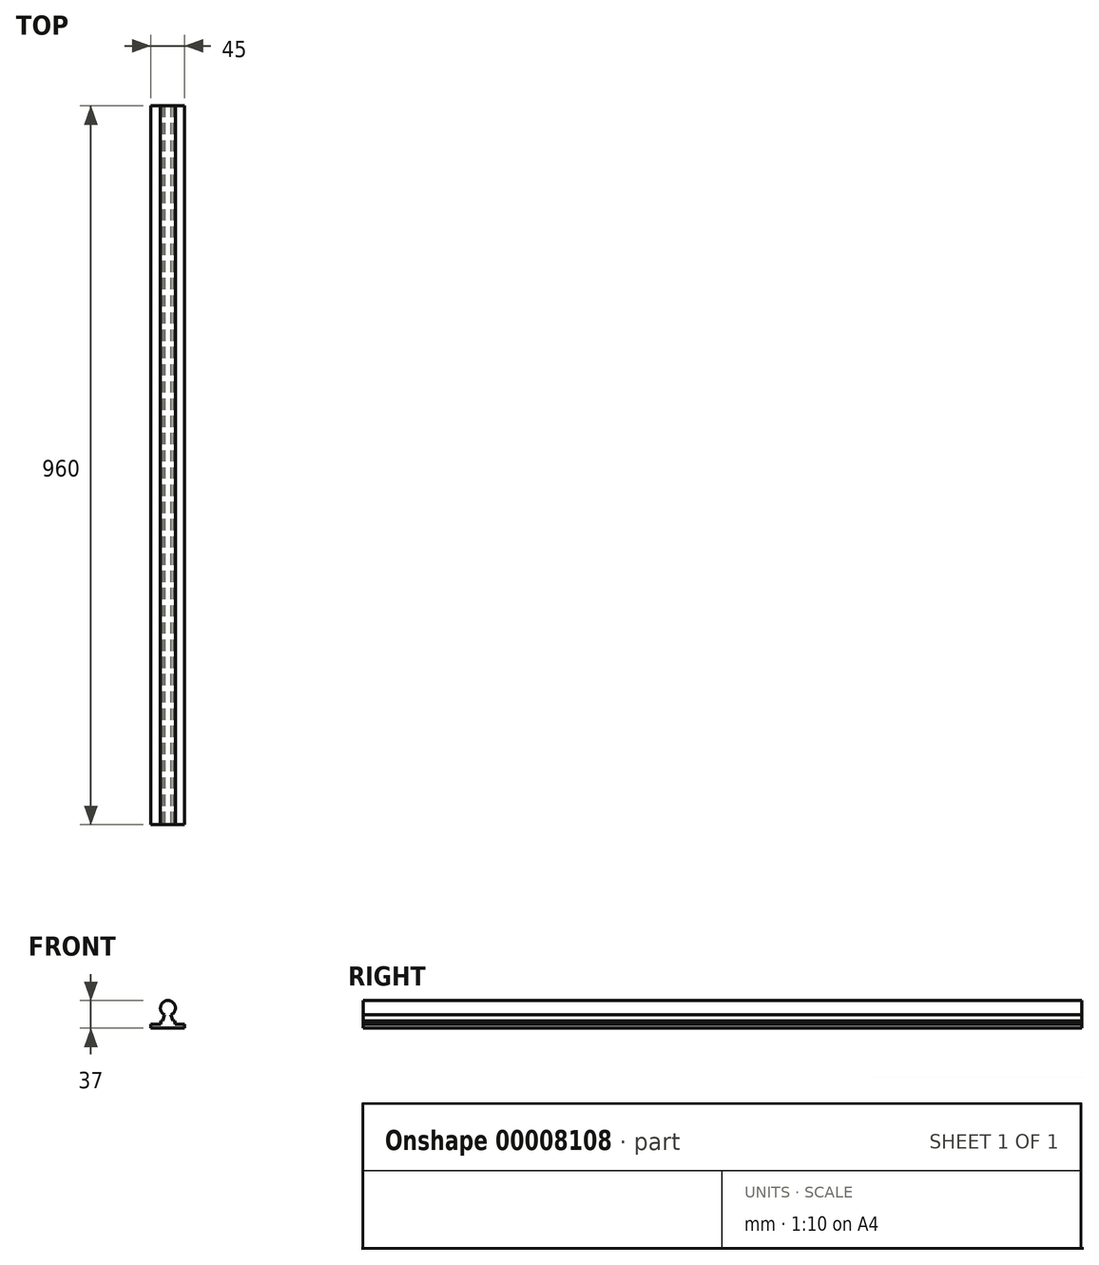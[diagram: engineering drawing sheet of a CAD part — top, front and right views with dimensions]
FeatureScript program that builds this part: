
annotation { "Feature Type Name" : "Feature", "Feature Type Description" : "" }
export const myFeature = defineFeature(function(context is Context, id is Id, definition is map)
    precondition{}
    {
        {
            var Q0;
            Q0=qCreatedBy(makeId("Front.planeOp"),FACE);
            var sketch = newSketch(context, id + "F0", { "sketchPlane" : qUnion([Q0])});
            skLineSegment(sketch, "E0", {"start": v(-29.77, 5.25) * mm, "end": v(15.23, 5.25) * mm});
            skLineSegment(sketch, "E1", {"start": v(15.23, 10.25) * mm, "end": v(2.23, 10.25) * mm});
            skLineSegment(sketch, "E2", {"start": v(2.23, 10.25) * mm, "end": v(2.23, 15.25) * mm});
            skLineSegment(sketch, "E3", {"start": v(-0.27, 15.25) * mm, "end": v(-3.23, 22.98) * mm});
            skLineSegment(sketch, "E4", {"start": v(-16.77, 10.25) * mm, "end": v(-16.77, 15.25) * mm});
            skLineSegment(sketch, "E5", {"start": v(-29.77, 10.25) * mm, "end": v(-16.77, 10.25) * mm});
            skLineSegment(sketch, "E6", {"start": v(-14.27, 15.25) * mm, "end": v(-11.22, 23.2) * mm});
            skCircle(sketch, "E7", {"center": v(-6.96, 32.25) * mm, "radius": 10 * mm});
            skLineSegment(sketch, "E8", {"start": v(15.23, 5.25) * mm, "end": v(15.23, 10.25) * mm});
            skLineSegment(sketch, "E9", {"start": v(-29.77, 5.25) * mm, "end": v(-29.77, 10.25) * mm});
            skLineSegment(sketch, "E10", {"start": v(-16.77, 15.25) * mm, "end": v(-14.27, 15.25) * mm});
            skLineSegment(sketch, "E11", {"start": v(2.23, 15.25) * mm, "end": v(-0.27, 15.25) * mm});
            skSolve(sketch);
        }
        {
            var Q0;
            Q0=makeQuery(id+"F0.imprint","IMPRINT",FACE,{"disambiguationData":[TD([[makeQuery(id+"F0.imprint","IMPRINT",EDGE,{"derivedFrom":sQuery(id+"F0.wireOp",EDGE,"E0")}),1.0]])]});
            var Q1;
            {var subQ0=sQuery(id+"F0.wireOp",EDGE,"E7");var subQ2=makeQuery(id+"F0.imprint","INTERSECT",VERTEX,{"derivedFrom":[sQuery(id+"F0.wireOp",EDGE,"E3"),subQ0]});Q1=makeQuery(id+"F0.imprint","IMPRINT",FACE,{"disambiguationData":[TD([[makeQuery(id+"F0.imprint","IMPRINT",EDGE,{"disambiguationData":[TD([[subQ2,1.0]])],"derivedFrom":subQ0}),1.0]])]});}
            extrude(context, id + "F1", {"entities" : qUnion([Q0, Q1]), "oppositeDirection" : true, "depth" : 960 * mm});
        }
    });
